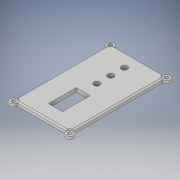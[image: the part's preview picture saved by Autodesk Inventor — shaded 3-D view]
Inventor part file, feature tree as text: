
AUTODESK INVENTOR PART (.ipt)
format: ipt  version: 2019 (Build 230136000, 136)  size: 197,120 bytes
history: native  units: mm
features: extrude x5, sketch x5, projected_geometry x2, chamfer x1
ambient origin geometry x8: Origin, YZ Plane, XZ Plane, XY Plane, X Axis, Y Axis, Z Axis, Center Point
bodies: Solid1 (feature_tree)
feature tree (13):
  extrude  "Extrusion1"  Depth=110.0mm
  extrude  "Extrusion2"  Depth=110.0mm
  extrude  "Extrusion3"  Depth=3.0mm
  extrude  "Extrusion4"  Depth=3.0mm TaperAngle=0.0deg
  extrude  "Extrusion5"  Depth=31.5mm
  chamfer  "Chamfer1"  Distance=24.0mm
  sketch  "Sketch1"  dims[d0=64.0mm d1=110.0mm]
  sketch  "Sketch2"  dims[d2=8.485mm d3=20.0mm d5=110.0mm d6=20.0mm d8=64.0mm]
  projected_geometry  "Projected Loop1"
  sketch  "Sketch3"  dims[d11=3.0mm d12=0.0mm d13=4.3mm]
  sketch  "Sketch4"  dims[d14=20.0mm d16=110.0mm d17=20.0mm d19=64.0mm d22=3.0mm d23=0.0mm]
  sketch  "Sketch5"  dims[d24=16.0mm d25=31.5mm d26=24.0mm d27=24.0mm d28=15.7mm d29=3.0mm d30=0.0mm d31=6.8mm d32=6.8mm d33=6.8mm d34=15.7mm d35=15.7mm d36=15.7mm d37=15.7mm d38=3.0mm d39=0.0mm d40=20.0mm d42=110.0mm d43=20.0mm d45=64.0mm d48=1.5mm d49=0.0mm d50=1.5mm d51=2.0mm d52=45.0deg]
  projected_geometry  "Projected Loop2"
